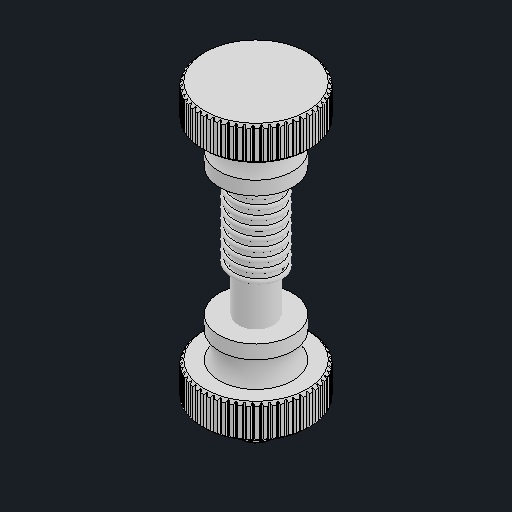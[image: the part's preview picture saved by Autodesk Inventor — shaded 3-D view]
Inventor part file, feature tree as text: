
AUTODESK INVENTOR PART (.ipt)
format: ipt  version: 2024.2 (Build 282272000, 272)  size: 1,076,224 bytes
history: native  units: mm
features: other x4, pattern_circular x1, chamfer x1, mirror x1, sweep x1
ambient origin geometry x8: Origin, YZ Plane, XZ Plane, XY Plane, X Axis, Y Axis, Z Axis, Center Point
bodies: Body1 (feature_tree), Body2 (feature_tree), Body3 (feature_tree), Body4 (feature_tree)
feature tree (8):
  other  "솔리드1"
  other  "솔리드2"
  other  "솔리드3"
  other  "솔리드4"
  pattern_circular  "CirPattern1"
  chamfer  "Chamfer2"  [1 undecoded]
  mirror  "Mirror2"
  sweep  "Sweep1"
note: 1 required parameter value undecoded (feature->parameter linkage not recoverable at this tier; creation-order binding heuristic only, values carry confidence <= 0.55)
